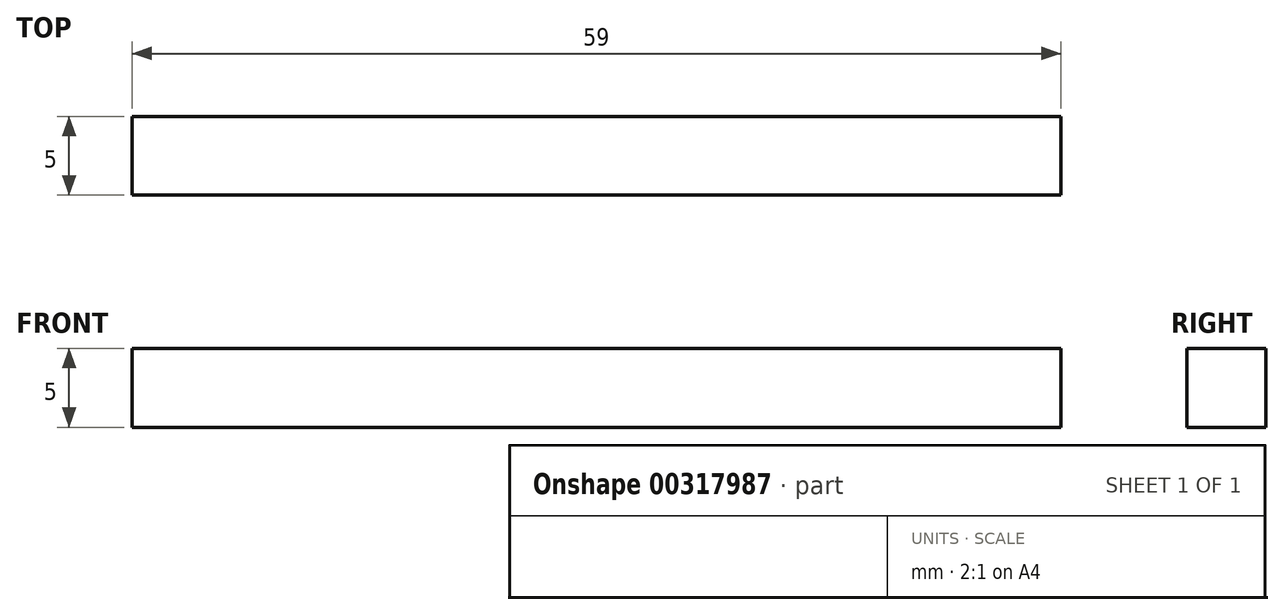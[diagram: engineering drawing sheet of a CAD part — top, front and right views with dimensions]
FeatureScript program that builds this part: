
annotation { "Feature Type Name" : "Feature", "Feature Type Description" : "" }
export const myFeature = defineFeature(function(context is Context, id is Id, definition is map)
    precondition{}
    {
        {
            var Q0;
            Q0=qCreatedBy(makeId("Front.planeOp"),FACE);
            var sketch = newSketch(context, id + "F0", { "sketchPlane" : qUnion([Q0])});
            skLineSegment(sketch, "E0.bottom", {"start": v(-29.5, 2.5) * mm, "end": v(29.5, 2.5) * mm});
            skLineSegment(sketch, "E0.top", {"start": v(-29.5, -2.5) * mm, "end": v(29.5, -2.5) * mm});
            skLineSegment(sketch, "E0.left", {"start": v(-29.5, 2.5) * mm, "end": v(-29.5, -2.5) * mm});
            skLineSegment(sketch, "E0.right", {"start": v(29.5, 2.5) * mm, "end": v(29.5, -2.5) * mm});
            skPoint(sketch, "E0.middle", {"position": v(0, 0) * mm});
            skSolve(sketch);
        }
        {
            var Q0;
            Q0=makeQuery(id+"F0.imprint","IMPRINT",FACE,{"disambiguationData":[TD([[makeQuery(id+"F0.imprint","IMPRINT",EDGE,{"derivedFrom":sQuery(id+"F0.wireOp",EDGE,"E0.bottom")}),-1.0]])]});
            extrude(context, id + "F1", {"entities" : qUnion([Q0]), "depth" : 5 * mm});
        }
    });
